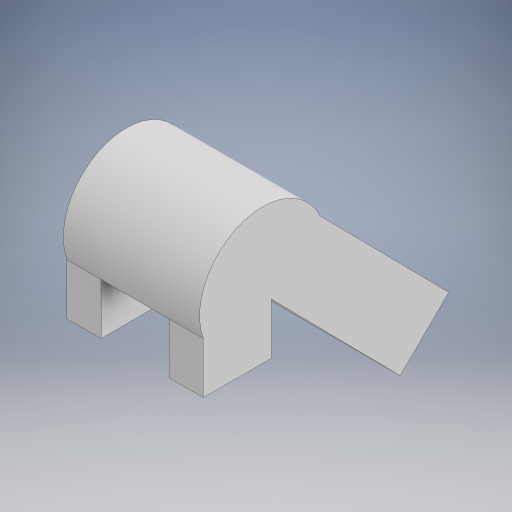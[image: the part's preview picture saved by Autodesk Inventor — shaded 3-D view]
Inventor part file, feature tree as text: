
AUTODESK INVENTOR PART (.ipt)
format: ipt  version: 2024.2 (Build 282272000, 272)  size: 266,240 bytes
history: native  units: in
note: dims shown in document units (in); Inventor stores cm internally (conversion verified against a paired STEP export)
features: extrude x2, sketch x2, plane x1, mirror x1
ambient origin geometry x8: Origin, YZ Plane, XZ Plane, XY Plane, X Axis, Y Axis, Z Axis, Center Point
bodies: Solid1 (feature_tree)
feature tree (6):
  extrude  "Extrusion1"  Depth=1.0in
  plane  "Work Plane1"
  mirror  "Mirror1"
  extrude  "Extrusion2"  Depth=0.5in TaperAngle=0.0deg
  sketch  "Sketch1"  dims[d0=0.75in d1=1.0in]
  sketch  "Sketch2"  dims[d2=1.0in d3=0.5in d4=0.0in d5=0.5in d6=0.5in d7=0.0in]
